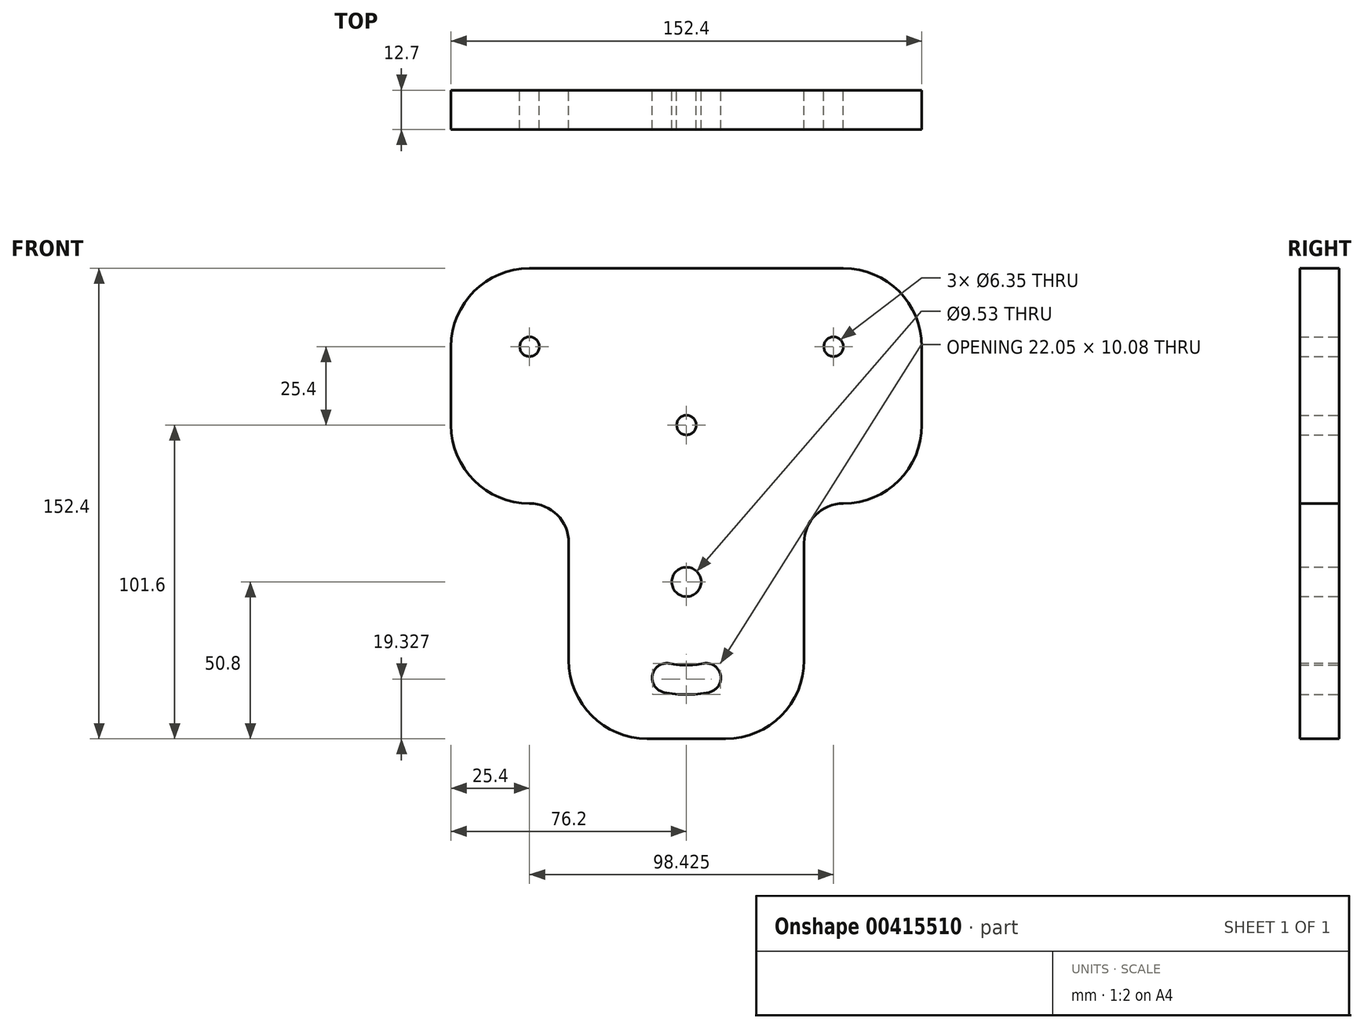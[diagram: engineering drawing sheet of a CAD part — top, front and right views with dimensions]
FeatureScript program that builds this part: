
annotation { "Feature Type Name" : "Feature", "Feature Type Description" : "" }
export const myFeature = defineFeature(function(context is Context, id is Id, definition is map)
    precondition{}
    {
        {
            var Q0;
            Q0=qCreatedBy(makeId("Front.planeOp"),FACE);
            var sketch = newSketch(context, id + "F0", { "sketchPlane" : qUnion([Q0])});
            skLineSegment(sketch, "E0", {"start": v(-50.8, 0) * mm, "end": v(50.8, 0) * mm});
            skLineSegment(sketch, "E1", {"start": v(76.2, -25.4) * mm, "end": v(76.2, -50.8) * mm});
            skLineSegment(sketch, "E2", {"start": v(50.8, -76.2) * mm, "end": v(50.8, -76.2) * mm});
            skLineSegment(sketch, "E3", {"start": v(38.1, -88.9) * mm, "end": v(38.1, -127) * mm});
            skLineSegment(sketch, "E4", {"start": v(12.7, -152.4) * mm, "end": v(-12.7, -152.4) * mm});
            skLineSegment(sketch, "E5", {"start": v(-38.1, -127) * mm, "end": v(-38.1, -88.9) * mm});
            skLineSegment(sketch, "E6", {"start": v(-50.8, -76.2) * mm, "end": v(-50.8, -76.2) * mm});
            skLineSegment(sketch, "E7", {"start": v(-76.2, -50.8) * mm, "end": v(-76.2, -25.4) * mm});
            skLineSegment(sketch, "E8", {"start": v(0, -152.4) * mm, "end": v(0, 0) * mm, "construction": true});
            skCircle(sketch, "E9", {"center": v(0, -101.6) * mm, "radius": 4.76 * mm});
            skCircle(sketch, "E10", {"center": v(-50.8, -25.4) * mm, "radius": 3.18 * mm});
            skCircle(sketch, "E11", {"center": v(47.63, -25.4) * mm, "radius": 3.18 * mm});
            skCircle(sketch, "E12", {"center": v(0, -50.8) * mm, "radius": 3.18 * mm});
            skArc(sketch, "E13", {"start": v(-5.4, -128.04) * mm, "mid": v(0, -128.59) * mm, "end": v(5.4, -128.04) * mm});
            skArc(sketch, "E14", {"start": v(7.3, -137.37) * mm, "mid": v(0, -138.11) * mm, "end": v(-7.3, -137.37) * mm});
            skArc(sketch, "E15", {"start": v(7.3, -137.37) * mm, "mid": v(11.02, -131.76) * mm, "end": v(5.4, -128.04) * mm});
            skArc(sketch, "E16", {"start": v(-5.4, -128.04) * mm, "mid": v(-11.02, -131.76) * mm, "end": v(-7.3, -137.37) * mm});
            skPoint(sketch, "E17.visualSharp", {"position": v(-76.2, 0) * mm});
            skArc(sketch, "E17.filletArc", {"start": v(-50.8, 0) * mm, "mid": v(-68.76, -7.44) * mm, "end": v(-76.2, -25.4) * mm});
            skPoint(sketch, "E18.visualSharp", {"position": v(76.2, 0) * mm});
            skArc(sketch, "E18.filletArc", {"start": v(76.2, -25.4) * mm, "mid": v(68.76, -7.44) * mm, "end": v(50.8, 0) * mm});
            skPoint(sketch, "E19.visualSharp", {"position": v(-76.2, -76.2) * mm});
            skArc(sketch, "E19.filletArc", {"start": v(-76.2, -50.8) * mm, "mid": v(-68.76, -68.76) * mm, "end": v(-50.8, -76.2) * mm});
            skPoint(sketch, "E20.visualSharp", {"position": v(-38.1, -76.2) * mm});
            skArc(sketch, "E20.filletArc", {"start": v(-38.1, -88.9) * mm, "mid": v(-41.82, -79.92) * mm, "end": v(-50.8, -76.2) * mm});
            skPoint(sketch, "E21.visualSharp", {"position": v(38.1, -76.2) * mm});
            skArc(sketch, "E21.filletArc", {"start": v(50.8, -76.2) * mm, "mid": v(41.82, -79.92) * mm, "end": v(38.1, -88.9) * mm});
            skPoint(sketch, "E22.visualSharp", {"position": v(76.2, -76.2) * mm});
            skArc(sketch, "E22.filletArc", {"start": v(50.8, -76.2) * mm, "mid": v(68.76, -68.76) * mm, "end": v(76.2, -50.8) * mm});
            skPoint(sketch, "E23.visualSharp", {"position": v(-38.1, -152.4) * mm});
            skArc(sketch, "E23.filletArc", {"start": v(-38.1, -127) * mm, "mid": v(-30.66, -144.96) * mm, "end": v(-12.7, -152.4) * mm});
            skPoint(sketch, "E24.visualSharp", {"position": v(38.1, -152.4) * mm});
            skArc(sketch, "E24.filletArc", {"start": v(12.7, -152.4) * mm, "mid": v(30.66, -144.96) * mm, "end": v(38.1, -127) * mm});
            skSolve(sketch);
        }
        {
            var Q0;
            Q0=makeQuery(id+"F0.imprint","IMPRINT",FACE,{"disambiguationData":[TD([[makeQuery(id+"F0.imprint","IMPRINT",EDGE,{"derivedFrom":sQuery(id+"F0.wireOp",EDGE,"E0")}),-1.0]])]});
            extrude(context, id + "F1", {"entities" : qUnion([Q0]), "depth" : 12.7 * mm});
        }
    });
